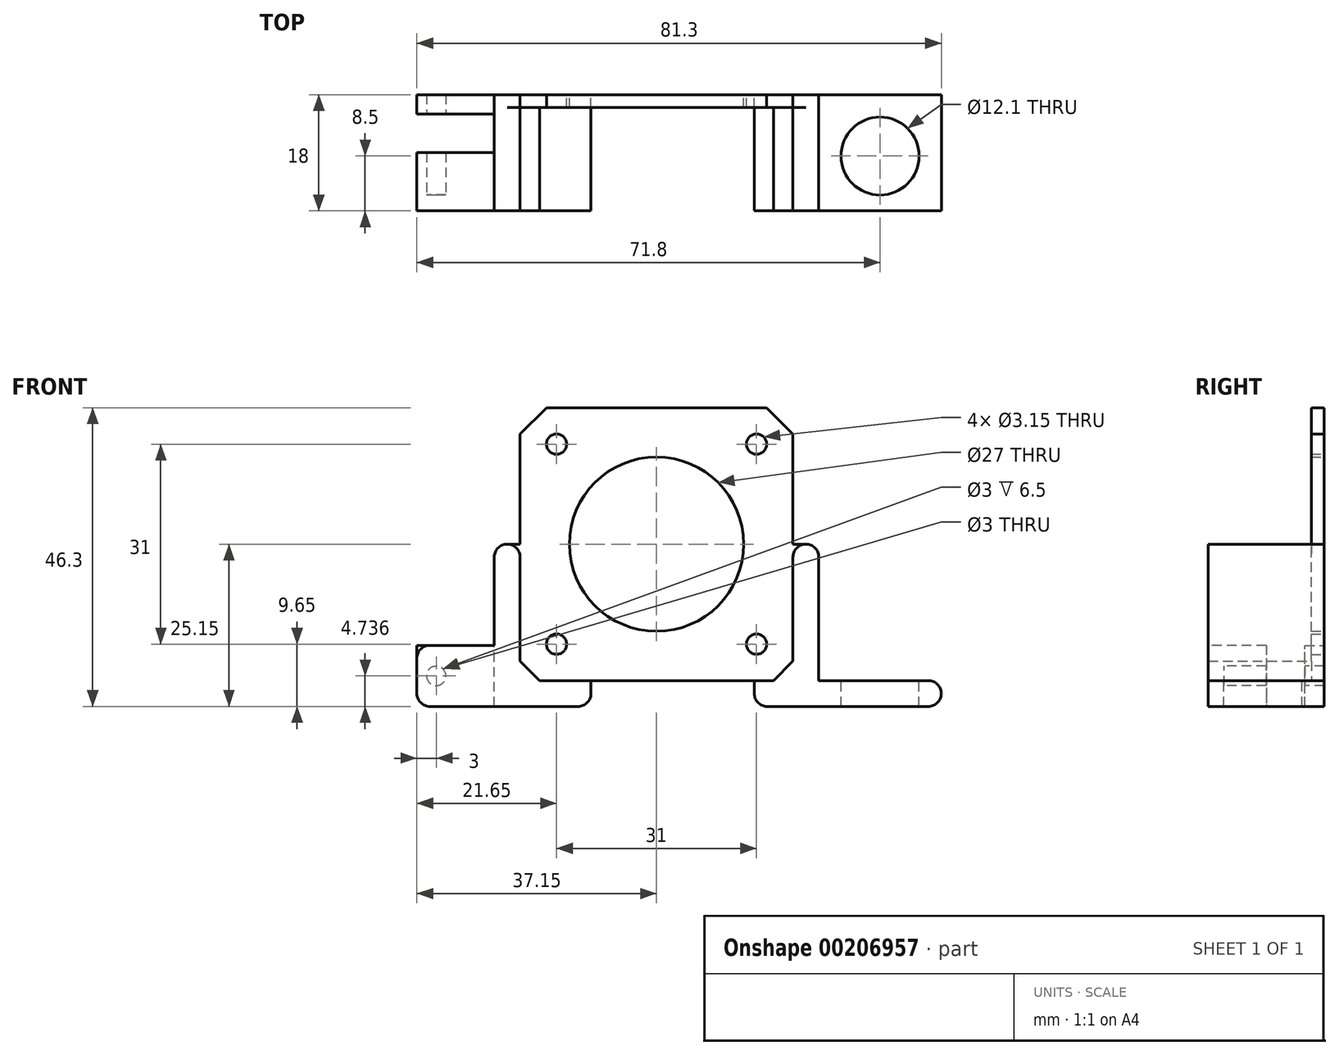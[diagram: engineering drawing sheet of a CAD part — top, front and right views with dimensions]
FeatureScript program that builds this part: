
annotation { "Feature Type Name" : "Feature", "Feature Type Description" : "" }
export const myFeature = defineFeature(function(context is Context, id is Id, definition is map)
    precondition{}
    {
        {
            var Q0;
            Q0=qCreatedBy(makeId("Front.planeOp"),FACE);
            var sketch = newSketch(context, id + "F0", { "sketchPlane" : qUnion([Q0])});
            skLineSegment(sketch, "E0.bottom", {"start": v(21.15, 21.15) * mm, "end": v(-21.15, 21.15) * mm});
            skLineSegment(sketch, "E0.top", {"start": v(21.15, -21.15) * mm, "end": v(-21.15, -21.15) * mm});
            skLineSegment(sketch, "E0.left", {"start": v(21.15, 21.15) * mm, "end": v(21.15, -21.15) * mm});
            skLineSegment(sketch, "E0.right", {"start": v(-21.15, 21.15) * mm, "end": v(-21.15, -21.15) * mm});
            skPoint(sketch, "E0.middle", {"position": v(0, 0) * mm});
            skCircle(sketch, "E1", {"center": v(0, 0) * mm, "radius": 13.5 * mm});
            skCircle(sketch, "E2", {"center": v(-15.5, 15.5) * mm, "radius": 1.57 * mm});
            skCircle(sketch, "E3.MirrorC", {"center": v(15.5, 15.5) * mm, "radius": 1.57 * mm});
            skCircle(sketch, "E4.MirrorC", {"center": v(-15.5, -15.5) * mm, "radius": 1.57 * mm});
            skCircle(sketch, "E5.MirrorC", {"center": v(15.5, -15.5) * mm, "radius": 1.57 * mm});
            skLineSegment(sketch, "E6", {"start": v(-21.15, 0) * mm, "end": v(-25.15, 0) * mm});
            skLineSegment(sketch, "E7", {"start": v(-25.15, 0) * mm, "end": v(-25.15, -25.15) * mm});
            skLineSegment(sketch, "E8", {"start": v(-25.15, -25.15) * mm, "end": v(25.15, -25.15) * mm});
            skLineSegment(sketch, "E9", {"start": v(25.15, -25.15) * mm, "end": v(25.15, 0) * mm});
            skLineSegment(sketch, "E10", {"start": v(25.15, 0) * mm, "end": v(21.15, 0) * mm});
            skLineSegment(sketch, "E11", {"start": v(-10.15, -21.15) * mm, "end": v(-10.15, -25.15) * mm});
            skLineSegment(sketch, "E12", {"start": v(15.15, -21.15) * mm, "end": v(15.15, -25.15) * mm});
            skLineSegment(sketch, "E13", {"start": v(-17.05, 21.15) * mm, "end": v(-21.15, 17.05) * mm});
            skLineSegment(sketch, "E14.MirrorCS", {"start": v(17.05, 21.15) * mm, "end": v(21.15, 17.05) * mm});
            skLineSegment(sketch, "E15", {"start": v(21.15, -21.15) * mm, "end": v(44.15, -21.15) * mm});
            skLineSegment(sketch, "E16", {"start": v(44.15, -21.15) * mm, "end": v(44.15, -25.15) * mm});
            skLineSegment(sketch, "E17", {"start": v(44.15, -25.15) * mm, "end": v(25.15, -25.15) * mm});
            skSolve(sketch);
        }
        {
            var Q0;
            Q0=makeQuery(id+"F0.imprint","IMPRINT",FACE,{"disambiguationData":[TD([[makeQuery(id+"F0.imprint","IMPRINT",EDGE,{"derivedFrom":sQuery(id+"F0.wireOp",EDGE,"E1")}),-1.0]])]});
            var Q1;
            {var subQ1=sQuery(id+"F0.wireOp",EDGE,"E6");Q1=makeQuery(id+"F0.imprint","IMPRINT",FACE,{"disambiguationData":[TD([[makeQuery(id+"F0.imprint","IMPRINT",EDGE,{"derivedFrom":subQ1}),1.0]])]});}
            var Q2;
            {var subQ0=sQuery(id+"F0.wireOp",EDGE,"E9");Q2=makeQuery(id+"F0.imprint","IMPRINT",FACE,{"disambiguationData":[TD([[makeQuery(id+"F0.imprint","IMPRINT",EDGE,{"derivedFrom":subQ0}),1.0]])]});}
            var Q3;
            {var subQ0=sQuery(id+"F0.wireOp",EDGE,"E12");Q3=makeQuery(id+"F0.imprint","IMPRINT",FACE,{"disambiguationData":[TD([[makeQuery(id+"F0.imprint","IMPRINT",EDGE,{"derivedFrom":subQ0}),1.0]])]});}
            var Q4;
            {var subQ4=sQuery(id+"F0.wireOp",EDGE,"E16");Q4=makeQuery(id+"F0.imprint","IMPRINT",FACE,{"disambiguationData":[TD([[makeQuery(id+"F0.imprint","IMPRINT",EDGE,{"derivedFrom":subQ4}),-1.0]])]});}
            extrude(context, id + "F1", {"entities" : qUnion([Q0, Q1, Q2, Q3, Q4]), "depth" : 2 * mm});
        }
        {
            var Q0;
            {var subQ2=sQuery(id+"F0.wireOp",EDGE,"E6");Q0=makeQuery(id+"F0.imprint","IMPRINT",FACE,{"disambiguationData":[TD([[makeQuery(id+"F0.imprint","IMPRINT",EDGE,{"derivedFrom":subQ2}),1.0]])]});}
            var Q1;
            {var subQ0=sQuery(id+"F0.wireOp",EDGE,"E12");Q1=makeQuery(id+"F0.imprint","IMPRINT",FACE,{"disambiguationData":[TD([[makeQuery(id+"F0.imprint","IMPRINT",EDGE,{"derivedFrom":subQ0}),1.0]])]});}
            var Q2;
            {var subQ4=sQuery(id+"F0.wireOp",EDGE,"E16");Q2=makeQuery(id+"F0.imprint","IMPRINT",FACE,{"disambiguationData":[TD([[makeQuery(id+"F0.imprint","IMPRINT",EDGE,{"derivedFrom":subQ4}),-1.0]])]});}
            var Q3;
            {var subQ3=sQuery(id+"F0.wireOp",EDGE,"E10");Q3=makeQuery(id+"F0.imprint","IMPRINT",FACE,{"disambiguationData":[TD([[makeQuery(id+"F0.imprint","IMPRINT",EDGE,{"derivedFrom":subQ3}),1.0]])]});}
            extrude(context, id + "F2", {"entities" : qUnion([Q0, Q1, Q2, Q3]), "operationType" : NewBodyOperationType.ADD, "depth" : 18 * mm});
        }
        {
            var Q0;
            {var subQ0=sQuery(id+"F0.wireOp",EDGE,"E15");Q0=makeQuery(id+"F2.boolean.opBoolean","MERGE",FACE,{"derivedFrom":[makeQuery(id+"F1.opExtrude","SWEPT_FACE",FACE,{"disambiguationData":[OSD([subQ0])]}),makeQuery(id+"F2.opExtrude","SWEPT_FACE",FACE,{"disambiguationData":[OSD([subQ0])]})]});}
            var sketch = newSketch(context, id + "F3", { "sketchPlane" : qUnion([Q0])});
            skCircle(sketch, "E18", {"center": v(34.65, -9.5) * mm, "radius": 6.05 * mm});
            skSolve(sketch);
        }
        {
            var Q0;
            {var subQ0=sQuery(id+"F0.wireOp",EDGE,"E7");Q0=makeQuery(id+"F2.boolean.opBoolean","MERGE",FACE,{"derivedFrom":[makeQuery(id+"F1.opExtrude","SWEPT_FACE",FACE,{"disambiguationData":[OSD([subQ0])]}),makeQuery(id+"F2.opExtrude","SWEPT_FACE",FACE,{"disambiguationData":[OSD([subQ0])]})]});}
            var sketch = newSketch(context, id + "F4", { "sketchPlane" : qUnion([Q0])});
            skLineSegment(sketch, "E19", {"start": v(3, -25.15) * mm, "end": v(3, -15.68) * mm});
            skLineSegment(sketch, "E20", {"start": v(3, -15.68) * mm, "end": v(0, -15.68) * mm});
            skLineSegment(sketch, "E21", {"start": v(0, -15.68) * mm, "end": v(18, -15.68) * mm});
            skLineSegment(sketch, "E22", {"start": v(9, -15.68) * mm, "end": v(9, -25.15) * mm});
            skSolve(sketch);
        }
        {
            var Q0;
            Q0 = qSketchRegion(id + "F4", true);
            var Q1;
            {var subQ0=sQuery(id+"F4.wireOp",EDGE,"E19");Q1=makeQuery(id+"F4.imprint","IMPRINT",FACE,{"disambiguationData":[TD([[makeQuery(id+"F4.imprint","IMPRINT",EDGE,{"derivedFrom":subQ0}),1.0]])]});}
            var Q2;
            {var subQ4=sQuery(id+"F4.wireOp",EDGE,"E22");Q2=makeQuery(id+"F4.imprint","IMPRINT",FACE,{"disambiguationData":[TD([[makeQuery(id+"F4.imprint","IMPRINT",EDGE,{"derivedFrom":subQ4}),1.0]])]});}
            extrude(context, id + "F5", {"entities" : qUnion([Q0, Q1, Q2]), "operationType" : NewBodyOperationType.ADD, "depth" : 12 * mm});
        }
        {
            var Q0;
            Q0=makeQuery(id+"F5.opExtrude","SWEPT_FACE",FACE,{"disambiguationData":[OSD([sQuery(id+"F4.wireOp",EDGE,"E19")])]});
            var sketch = newSketch(context, id + "F6", { "sketchPlane" : qUnion([Q0])});
            skCircle(sketch, "E23", {"center": v(-34.15, -20.41) * mm, "radius": 1.5 * mm});
            skPoint(sketch, "E23.centerSnap0", {"position": v(-37.15, -20.41) * mm});
            skSolve(sketch);
        }
        {
            var Q0;
            Q0 = qSketchRegion(id + "F6", true);
            extrude(context, id + "F7", {"entities" : qUnion([Q0]), "operationType" : NewBodyOperationType.REMOVE, "oppositeDirection" : true, "depth" : 25 * mm, "symmetric" : true});
        }
        {
            var Q0;
            Q0=makeQuery(id+"F3.imprint","IMPRINT",FACE,{"disambiguationData":[TD([[makeQuery(id+"F3.imprint","IMPRINT",EDGE,{"derivedFrom":sQuery(id+"F3.wireOp",EDGE,"E18")}),1.0]])]});
            extrude(context, id + "F8", {"entities" : qUnion([Q0]), "operationType" : NewBodyOperationType.REMOVE, "oppositeDirection" : true, "depth" : 25 * mm});
        }
        {
            var Q0;
            {var subQ0=sQuery(id+"F4.wireOp",EDGE,"E21");Q0=makeQuery(id+"F5.opExtrude","CAP_EDGE",EDGE,{"disambiguationData":[OSD([subQ0]),TDD([makeQuery(id+"F4.imprint","IMPRINT",EDGE,{"disambiguationData":[TD([[makeQuery(id+"F4.imprint","INTERSECT",VERTEX,{"derivedFrom":[sQuery(id+"F4.wireOp",EDGE,"E19"),subQ0]}),1.0]])],"derivedFrom":subQ0})])],"isStart":true});}
            var Q1;
            {var subQ0=sQuery(id+"F4.wireOp",EDGE,"E21");Q1=makeQuery(id+"F5.opExtrude","CAP_EDGE",EDGE,{"disambiguationData":[OSD([subQ0]),TDD([makeQuery(id+"F4.imprint","IMPRINT",EDGE,{"disambiguationData":[TD([[makeQuery(id+"F4.imprint","INTERSECT",VERTEX,{"derivedFrom":[sQuery(id+"F4.wireOp",EDGE,"E19"),subQ0]}),1.0]])],"derivedFrom":subQ0})])],"isStart":false});}
            var Q2;
            {var subQ0=sQuery(id+"F0.wireOp",EDGE,"E8");var subQ1=sQuery(id+"F0.wireOp",EDGE,"E7");var subQ2=makeQuery(id+"F2.boolean.opBoolean","MERGE",EDGE,{"derivedFrom":[makeQuery(id+"F1.opExtrude","SWEPT_EDGE",EDGE,{"disambiguationData":[OSD([subQ1,subQ0])]}),makeQuery(id+"F2.opExtrude","SWEPT_EDGE",EDGE,{"disambiguationData":[OSD([subQ1,subQ0])]})]});Q2=makeQuery(id+"F5.opExtrude","CAP_EDGE",EDGE,{"disambiguationData":[OSD([subQ1,subQ0]),TDD([makeQuery(id+"F4.imprint","IMPRINT",EDGE,{"disambiguationData":[TD([[makeQuery(id+"F4.imprint","INTERSECT",VERTEX,{"derivedFrom":[makeQuery(id+"F1.opExtrude","CAP_EDGE",EDGE,{"disambiguationData":[OSD([subQ1])],"isStart":true}),subQ2]}),1.0]])],"derivedFrom":subQ2})])],"isStart":false});}
            var Q3;
            {var subQ0=sQuery(id+"F4.wireOp",EDGE,"E21");Q3=makeQuery(id+"F5.opExtrude","CAP_EDGE",EDGE,{"disambiguationData":[OSD([subQ0]),TDD([makeQuery(id+"F4.imprint","IMPRINT",EDGE,{"disambiguationData":[TD([[makeQuery(id+"F4.imprint","INTERSECT",VERTEX,{"derivedFrom":[makeQuery(id+"F2.opExtrude","CAP_EDGE",EDGE,{"disambiguationData":[OSD([sQuery(id+"F0.wireOp",EDGE,"E7")])],"isStart":false}),subQ0]}),1.0]])],"derivedFrom":subQ0})])],"isStart":false});}
            var Q4;
            {var subQ0=sQuery(id+"F0.wireOp",EDGE,"E8");var subQ1=sQuery(id+"F0.wireOp",EDGE,"E7");var subQ2=makeQuery(id+"F2.boolean.opBoolean","MERGE",EDGE,{"derivedFrom":[makeQuery(id+"F1.opExtrude","SWEPT_EDGE",EDGE,{"disambiguationData":[OSD([subQ1,subQ0])]}),makeQuery(id+"F2.opExtrude","SWEPT_EDGE",EDGE,{"disambiguationData":[OSD([subQ1,subQ0])]})]});Q4=makeQuery(id+"F5.opExtrude","CAP_EDGE",EDGE,{"disambiguationData":[OSD([subQ1,subQ0]),TDD([makeQuery(id+"F4.imprint","IMPRINT",EDGE,{"disambiguationData":[TD([[makeQuery(id+"F4.imprint","INTERSECT",VERTEX,{"derivedFrom":[makeQuery(id+"F2.opExtrude","CAP_EDGE",EDGE,{"disambiguationData":[OSD([subQ1])],"isStart":false}),subQ2]}),-1.0]])],"derivedFrom":subQ2})])],"isStart":false});}
            var Q5;
            {var subQ0=sQuery(id+"F4.wireOp",EDGE,"E21");Q5=makeQuery(id+"F5.opExtrude","CAP_EDGE",EDGE,{"disambiguationData":[OSD([subQ0]),TDD([makeQuery(id+"F4.imprint","IMPRINT",EDGE,{"disambiguationData":[TD([[makeQuery(id+"F4.imprint","INTERSECT",VERTEX,{"derivedFrom":[makeQuery(id+"F2.opExtrude","CAP_EDGE",EDGE,{"disambiguationData":[OSD([sQuery(id+"F0.wireOp",EDGE,"E7")])],"isStart":false}),subQ0]}),1.0]])],"derivedFrom":subQ0})])],"isStart":true});}
            var Q6;
            {var subQ0=sQuery(id+"F0.wireOp",EDGE,"E11");var subQ1=sQuery(id+"F0.wireOp",EDGE,"E8");Q6=makeQuery(id+"F2.boolean.opBoolean","MERGE",EDGE,{"derivedFrom":[makeQuery(id+"F1.opExtrude","SWEPT_EDGE",EDGE,{"disambiguationData":[OSD([subQ1,subQ0])]}),makeQuery(id+"F2.opExtrude","SWEPT_EDGE",EDGE,{"disambiguationData":[OSD([subQ1,subQ0])]})]});}
            var Q7;
            {var subQ0=sQuery(id+"F0.wireOp",EDGE,"E12");var subQ1=sQuery(id+"F0.wireOp",EDGE,"E8");Q7=makeQuery(id+"F2.boolean.opBoolean","MERGE",EDGE,{"derivedFrom":[makeQuery(id+"F1.opExtrude","SWEPT_EDGE",EDGE,{"disambiguationData":[OSD([subQ1,subQ0])]}),makeQuery(id+"F2.opExtrude","SWEPT_EDGE",EDGE,{"disambiguationData":[OSD([subQ1,subQ0])]})]});}
            var Q8;
            {var subQ0=sQuery(id+"F0.wireOp",EDGE,"E17");var subQ1=sQuery(id+"F0.wireOp",EDGE,"E16");Q8=makeQuery(id+"F2.boolean.opBoolean","MERGE",EDGE,{"derivedFrom":[makeQuery(id+"F1.opExtrude","SWEPT_EDGE",EDGE,{"disambiguationData":[OSD([subQ1,subQ0])]}),makeQuery(id+"F2.opExtrude","SWEPT_EDGE",EDGE,{"disambiguationData":[OSD([subQ1,subQ0])]})]});}
            var Q9;
            {var subQ0=sQuery(id+"F0.wireOp",EDGE,"E16");var subQ1=sQuery(id+"F0.wireOp",EDGE,"E15");Q9=makeQuery(id+"F2.boolean.opBoolean","MERGE",EDGE,{"derivedFrom":[makeQuery(id+"F1.opExtrude","SWEPT_EDGE",EDGE,{"disambiguationData":[OSD([subQ1,subQ0])]}),makeQuery(id+"F2.opExtrude","SWEPT_EDGE",EDGE,{"disambiguationData":[OSD([subQ1,subQ0])]})]});}
            var Q10;
            {var subQ0=sQuery(id+"F0.wireOp",EDGE,"E10");var subQ1=sQuery(id+"F0.wireOp",EDGE,"E9");Q10=makeQuery(id+"F2.boolean.opBoolean","MERGE",EDGE,{"derivedFrom":[makeQuery(id+"F1.opExtrude","SWEPT_EDGE",EDGE,{"disambiguationData":[OSD([subQ1,subQ0])]}),makeQuery(id+"F2.opExtrude","SWEPT_EDGE",EDGE,{"disambiguationData":[OSD([subQ1,subQ0])]})]});}
            var Q11;
            Q11=makeQuery(id+"F2.opExtrude","SWEPT_EDGE",EDGE,{"disambiguationData":[OSD([sQuery(id+"F0.wireOp",EDGE,"E0.left"),sQuery(id+"F0.wireOp",EDGE,"E10")])]});
            var Q12;
            Q12=makeQuery(id+"F2.opExtrude","SWEPT_EDGE",EDGE,{"disambiguationData":[OSD([sQuery(id+"F0.wireOp",EDGE,"E0.right"),sQuery(id+"F0.wireOp",EDGE,"E6")])]});
            var Q13;
            {var subQ0=sQuery(id+"F0.wireOp",EDGE,"E7");var subQ1=sQuery(id+"F0.wireOp",EDGE,"E6");Q13=makeQuery(id+"F2.boolean.opBoolean","MERGE",EDGE,{"derivedFrom":[makeQuery(id+"F1.opExtrude","SWEPT_EDGE",EDGE,{"disambiguationData":[OSD([subQ1,subQ0])]}),makeQuery(id+"F2.opExtrude","SWEPT_EDGE",EDGE,{"disambiguationData":[OSD([subQ1,subQ0])]})]});}
            fillet(context, id + "F9", {"entities" : qUnion([Q0, Q1, Q2, Q3, Q4, Q5, Q6, Q7, Q8, Q9, Q10, Q11, Q12, Q13]), "radius" : 2 * mm, "tangentPropagation" : true, "allowEdgeOverflow" : false});
        }
        {
            var Q0;
            Q0=makeQuery(id+"F2.opExtrude","SWEPT_EDGE",EDGE,{"disambiguationData":[OSD([sQuery(id+"F0.wireOp",EDGE,"E0.top"),sQuery(id+"F0.wireOp",EDGE,"E0.left"),sQuery(id+"F0.wireOp",EDGE,"E15")])]});
            var Q1;
            Q1=makeQuery(id+"F2.opExtrude","SWEPT_EDGE",EDGE,{"disambiguationData":[OSD([sQuery(id+"F0.wireOp",EDGE,"E0.top"),sQuery(id+"F0.wireOp",EDGE,"E0.right")])]});
            chamfer(context, id + "F10", {"entities" : qUnion([Q0, Q1]), "width" : 3 * mm, "tangentPropagation" : true});
        }
    });
